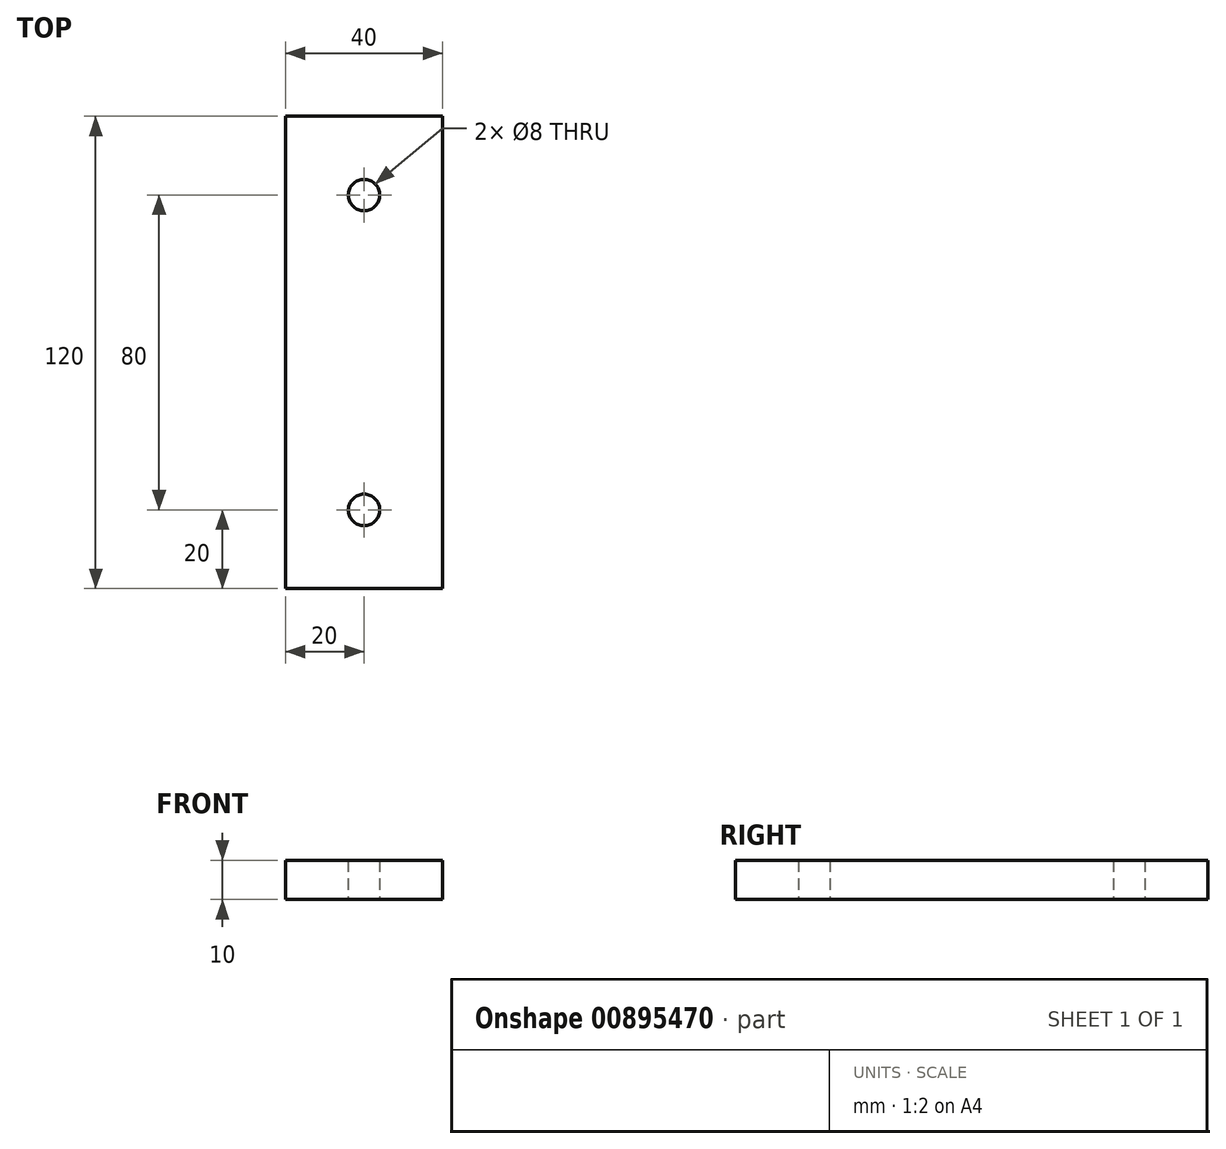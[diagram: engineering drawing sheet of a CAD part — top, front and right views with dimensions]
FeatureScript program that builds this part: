
annotation { "Feature Type Name" : "Feature", "Feature Type Description" : "" }
export const myFeature = defineFeature(function(context is Context, id is Id, definition is map)
    precondition{}
    {
        {
            var Q0;
            Q0=qCreatedBy(makeId("Top.planeOp"),FACE);
            var sketch = newSketch(context, id + "F0", { "sketchPlane" : qUnion([Q0])});
            skLineSegment(sketch, "E0.bottom", {"start": v(20, -60) * mm, "end": v(-20, -60) * mm});
            skLineSegment(sketch, "E0.top", {"start": v(20, 60) * mm, "end": v(-20, 60) * mm});
            skLineSegment(sketch, "E0.left", {"start": v(20, -60) * mm, "end": v(20, 60) * mm});
            skLineSegment(sketch, "E0.right", {"start": v(-20, -60) * mm, "end": v(-20, 60) * mm});
            skPoint(sketch, "E0.middle", {"position": v(0, 0) * mm});
            skCircle(sketch, "E1", {"center": v(0, 40) * mm, "radius": 4 * mm});
            skLineSegment(sketch, "E2", {"start": v(0.47, 0) * mm, "end": v(11.43, 0) * mm, "construction": true});
            skCircle(sketch, "E3.MirrorC", {"center": v(0, -40) * mm, "radius": 4 * mm});
            skSolve(sketch);
        }
        {
            var Q0;
            Q0 = qSketchRegion(id + "F0", true);
            extrude(context, id + "F1", {"entities" : qUnion([Q0]), "depth" : 10 * mm, "offsetDistance" : 25 * mm});
        }
    });
